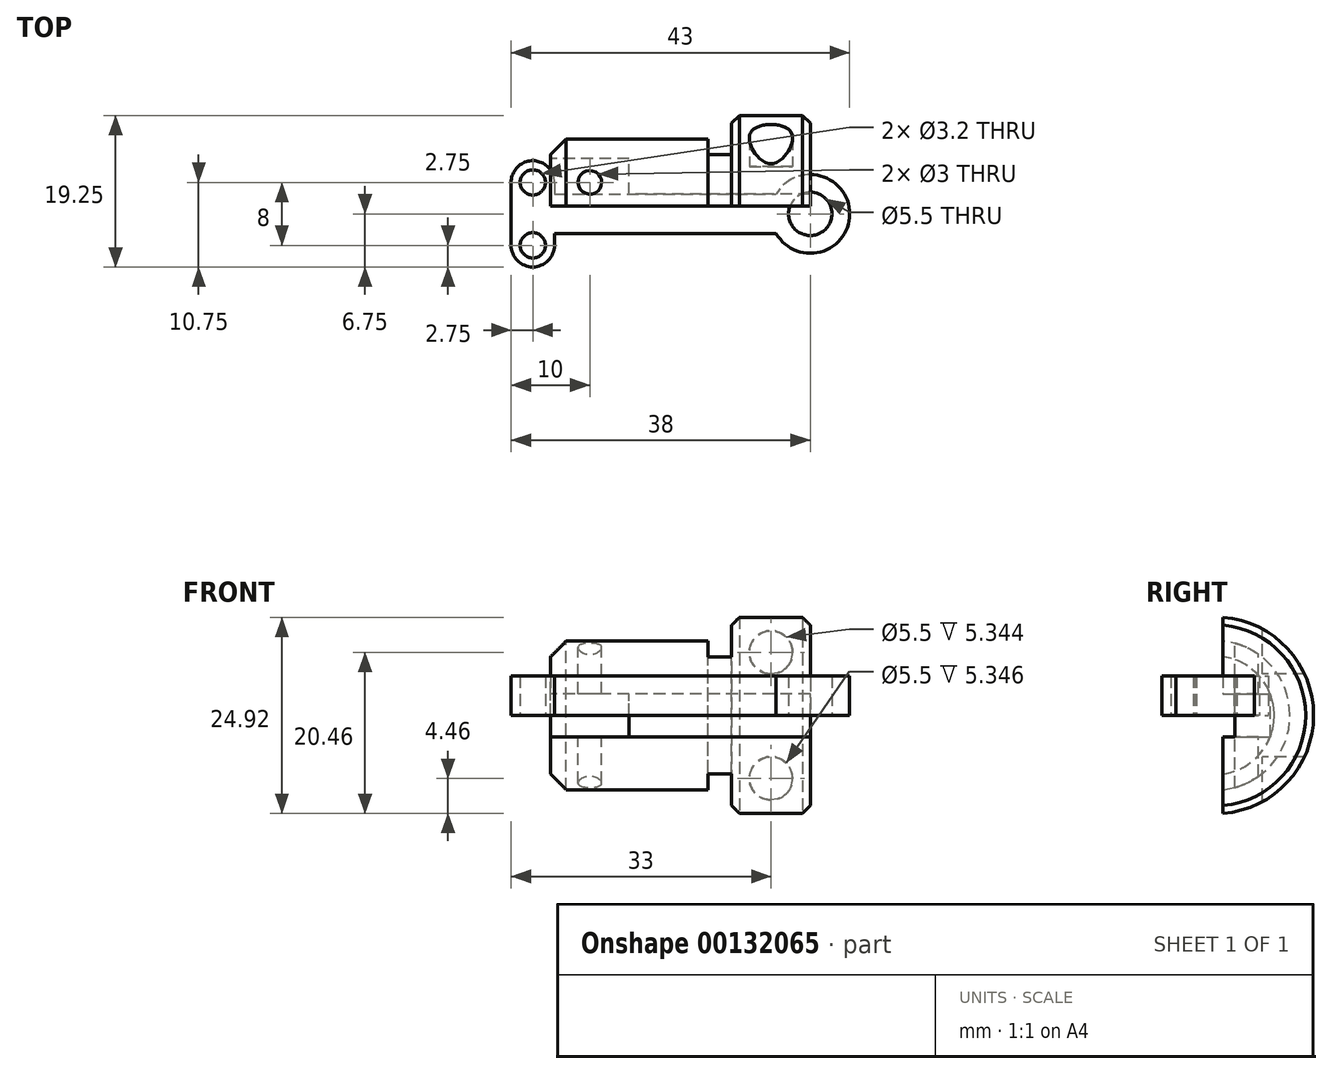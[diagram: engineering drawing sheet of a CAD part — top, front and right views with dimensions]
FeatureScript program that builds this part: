
annotation { "Feature Type Name" : "Feature", "Feature Type Description" : "" }
export const myFeature = defineFeature(function(context is Context, id is Id, definition is map)
    precondition{}
    {
        {
            var Q0;
            Q0=qCreatedBy(makeId("Front.planeOp"),FACE);
            var sketch = newSketch(context, id + "F0", { "sketchPlane" : qUnion([Q0])});
            skLineSegment(sketch, "E0", {"start": v(0, 0) * mm, "end": v(-33, 0) * mm});
            skLineSegment(sketch, "E1", {"start": v(-33, 0) * mm, "end": v(-33, 9.5) * mm});
            skLineSegment(sketch, "E2", {"start": v(-33, 9.5) * mm, "end": v(-13, 9.5) * mm});
            skLineSegment(sketch, "E3", {"start": v(-10, 12.5) * mm, "end": v(0, 12.5) * mm});
            skLineSegment(sketch, "E4", {"start": v(0, 12.5) * mm, "end": v(0, 0) * mm});
            skLineSegment(sketch, "E5", {"start": v(-13, 9.5) * mm, "end": v(-13, 7.5) * mm});
            skLineSegment(sketch, "E6", {"start": v(-13, 7.5) * mm, "end": v(-10, 7.5) * mm});
            skLineSegment(sketch, "E7", {"start": v(-10, 12.5) * mm, "end": v(-10, 7.5) * mm});
            skSolve(sketch);
        }
        {
            var Q0;
            Q0=makeQuery(id+"F0.imprint","IMPRINT",FACE,{"disambiguationData":[TD([[makeQuery(id+"F0.imprint","IMPRINT",EDGE,{"derivedFrom":sQuery(id+"F0.wireOp",EDGE,"E0")}),-1.0]])]});
            var Q1;
            Q1=sQuery(id+"F0.wireOp",EDGE,"E0");
            revolve(context, id + "F1", {"entities" : qUnion([Q0]), "axis" : qUnion([Q1]), "revolveType" : RevolveType.ONE_DIRECTION, "angle" : 180 * degree});
        }
        {
            var Q0;
            Q0=makeQuery(id+"F1.opRevolve","SWEPT_FACE",FACE,{"disambiguationData":[OSD([sQuery(id+"F0.wireOp",EDGE,"E4")])]});
            var sketch = newSketch(context, id + "F2", { "sketchPlane" : qUnion([Q0])});
            skLineSegment(sketch, "E8.bottom", {"start": v(0, 12.5) * mm, "end": v(1, 12.5) * mm});
            skLineSegment(sketch, "E8.top", {"start": v(0, -17.5) * mm, "end": v(1, -17.5) * mm});
            skLineSegment(sketch, "E8.left", {"start": v(0, 12.5) * mm, "end": v(0, -17.5) * mm});
            skLineSegment(sketch, "E8.right", {"start": v(1, 12.5) * mm, "end": v(1, -17.5) * mm});
            skSolve(sketch);
        }
        {
            var Q0;
            {var subQ0=sQuery(id+"F2.wireOp",EDGE,"E8.left");Q0=makeQuery(id+"F2.imprint","IMPRINT",FACE,{"disambiguationData":[TD([[makeQuery(id+"F2.imprint","IMPRINT",EDGE,{"derivedFrom":subQ0}),-1.0]])]});}
            extrude(context, id + "F3", {"entities" : qUnion([Q0]), "operationType" : NewBodyOperationType.REMOVE, "endBound" : BoundingType.THROUGH_ALL, "oppositeDirection" : true, "depth" : 25 * mm});
        }
        {
            var Q0;
            Q0=makeQuery(id+"F1.opRevolve","SWEPT_FACE",FACE,{"disambiguationData":[OSD([sQuery(id+"F0.wireOp",EDGE,"E1")])]});
            var sketch = newSketch(context, id + "F4", { "sketchPlane" : qUnion([Q0])});
            skLineSegment(sketch, "E9.bottom", {"start": v(-1, -2.75) * mm, "end": v(-7, -2.75) * mm});
            skLineSegment(sketch, "E9.top", {"start": v(-1, 2.75) * mm, "end": v(-7, 2.75) * mm});
            skLineSegment(sketch, "E9.left", {"start": v(-1, -2.75) * mm, "end": v(-1, 2.75) * mm});
            skLineSegment(sketch, "E9.right", {"start": v(-7, -2.75) * mm, "end": v(-7, 2.75) * mm});
            skSolve(sketch);
        }
        {
            var Q0;
            Q0=makeQuery(id+"F4.imprint","IMPRINT",FACE,{"disambiguationData":[TD([[makeQuery(id+"F4.imprint","IMPRINT",EDGE,{"derivedFrom":sQuery(id+"F4.wireOp",EDGE,"E9.bottom")}),-1.0]])]});
            extrude(context, id + "F5", {"entities" : qUnion([Q0]), "operationType" : NewBodyOperationType.REMOVE, "oppositeDirection" : true, "depth" : 10 * mm});
        }
        {
            var Q0;
            Q0=makeQuery(id+"F5.boolean.opBoolean","COPY",FACE,{"derivedFrom":makeQuery(id+"F5.opExtrude","CAP_FACE",FACE,{"disambiguationData":[OSD([sQuery(id+"F4.wireOp",EDGE,"E9.bottom"),sQuery(id+"F4.wireOp",EDGE,"E9.top"),sQuery(id+"F4.wireOp",EDGE,"E9.left"),sQuery(id+"F4.wireOp",EDGE,"E9.right")])],"isStart":false})});
            var sketch = newSketch(context, id + "F6", { "sketchPlane" : qUnion([Q0])});
            skLineSegment(sketch, "E10.bottom", {"start": v(-1, -2.75) * mm, "end": v(-2.5, -2.75) * mm});
            skLineSegment(sketch, "E10.top", {"start": v(-1, 2.75) * mm, "end": v(-4, 2.75) * mm});
            skLineSegment(sketch, "E10.left", {"start": v(-1, -2.75) * mm, "end": v(-1, 2.75) * mm});
            skLineSegment(sketch, "E10.right", {"start": v(-2.5, -2.75) * mm, "end": v(-2.5, 2.75) * mm});
            skSolve(sketch);
        }
        {
            var Q0;
            Q0=makeQuery(id+"F6.imprint","IMPRINT",FACE,{"disambiguationData":[TD([[makeQuery(id+"F6.imprint","IMPRINT",EDGE,{"derivedFrom":sQuery(id+"F6.wireOp",EDGE,"E10.bottom")}),-1.0]])]});
            extrude(context, id + "F7", {"entities" : qUnion([Q0]), "operationType" : NewBodyOperationType.REMOVE, "endBound" : BoundingType.THROUGH_ALL, "oppositeDirection" : true, "depth" : 25 * mm});
        }
        {
            var Q0;
            Q0=makeQuery(id+"F1.opRevolve","SWEPT_EDGE",EDGE,{"disambiguationData":[OSD([sQuery(id+"F0.wireOp",EDGE,"E1"),sQuery(id+"F0.wireOp",EDGE,"E2")])]});
            chamfer(context, id + "F8", {"entities" : qUnion([Q0]), "width" : 2 * mm, "tangentPropagation" : true});
        }
        {
            var Q0;
            Q0=qCreatedBy(makeId("Top.planeOp"),FACE);
            var sketch = newSketch(context, id + "F9", { "sketchPlane" : qUnion([Q0])});
            skCircle(sketch, "E11", {"center": v(-28, 4) * mm, "radius": 1.5 * mm});
            skSolve(sketch);
        }
        {
            var Q0;
            Q0 = qSketchRegion(id + "F9", true);
            extrude(context, id + "F10", {"entities" : qUnion([Q0]), "operationType" : NewBodyOperationType.REMOVE, "endBound" : BoundingType.SYMMETRIC, "oppositeDirection" : true, "depth" : 25 * mm});
        }
        {
            var Q0;
            Q0=qCreatedBy(makeId("Top.planeOp"),FACE);
            var sketch = newSketch(context, id + "F11", { "sketchPlane" : qUnion([Q0])});
            skArc(sketch, "E12", {"start": v(-4.33, -2.5) * mm, "mid": v(5, 0) * mm, "end": v(-4.33, 2.5) * mm});
            skCircle(sketch, "E13", {"center": v(0, 0) * mm, "radius": 2.75 * mm});
            skCircle(sketch, "E14", {"center": v(-35.25, 4) * mm, "radius": 1.6 * mm});
            skCircle(sketch, "E15", {"center": v(-35.25, -4) * mm, "radius": 1.6 * mm});
            skArc(sketch, "E16", {"start": v(-32.5, 4) * mm, "mid": v(-35.25, 6.75) * mm, "end": v(-38, 4) * mm});
            skArc(sketch, "E17", {"start": v(-38, -4) * mm, "mid": v(-35.25, -6.75) * mm, "end": v(-32.5, -4) * mm});
            skLineSegment(sketch, "E18", {"start": v(-38, 4) * mm, "end": v(-38, -4) * mm});
            skLineSegment(sketch, "E19", {"start": v(-32.5, 4) * mm, "end": v(-32.5, 2.5) * mm});
            skLineSegment(sketch, "E20", {"start": v(-32.5, -2.5) * mm, "end": v(-32.5, -4) * mm});
            skLineSegment(sketch, "E21.trimOffspring", {"start": v(-32.5, 2.5) * mm, "end": v(-4.33, 2.5) * mm});
            skLineSegment(sketch, "E22.trimOffspring", {"start": v(-32.5, -2.5) * mm, "end": v(-4.33, -2.5) * mm});
            skSolve(sketch);
        }
        {
            var Q0;
            Q0=makeQuery(id+"F11.imprint","IMPRINT",FACE,{"disambiguationData":[TD([[makeQuery(id+"F11.imprint","IMPRINT",EDGE,{"derivedFrom":sQuery(id+"F11.wireOp",EDGE,"E12")}),1.0]])]});
            extrude(context, id + "F12", {"entities" : qUnion([Q0]), "depth" : 5 * mm});
        }
        {
            var Q0;
            Q0=makeQuery(id+"F1.opRevolve","SWEPT_EDGE",EDGE,{"disambiguationData":[OSD([sQuery(id+"F0.wireOp",EDGE,"E3"),sQuery(id+"F0.wireOp",EDGE,"E7")])]});
            var Q1;
            Q1=makeQuery(id+"F1.opRevolve","SWEPT_EDGE",EDGE,{"disambiguationData":[OSD([sQuery(id+"F0.wireOp",EDGE,"E3"),sQuery(id+"F0.wireOp",EDGE,"E4")])]});
            chamfer(context, id + "F13", {"entities" : qUnion([Q0, Q1]), "width" : 1 * mm, "tangentPropagation" : true});
        }
        {
            var Q0;
            Q0=qCreatedBy(makeId("Front.planeOp"),FACE);
            cPlane(context, id + "F14", {"entities" : qUnion([Q0]), "cplaneType" : CPlaneType.OFFSET, "offset" : 6 * mm, "oppositeDirection" : true, "width" : 150 * mm, "height" : 150 * mm});
        }
        {
            var Q0;
            Q0=qCreatedBy(id+"F14.planeOp",FACE);
            var sketch = newSketch(context, id + "F15", { "sketchPlane" : qUnion([Q0])});
            skCircle(sketch, "E23", {"center": v(-5, -8) * mm, "radius": 2.75 * mm});
            skCircle(sketch, "E24", {"center": v(-5, 8) * mm, "radius": 2.75 * mm});
            skSolve(sketch);
        }
        {
            var Q0;
            Q0 = qSketchRegion(id + "F15", true);
            extrude(context, id + "F16", {"entities" : qUnion([Q0]), "operationType" : NewBodyOperationType.REMOVE, "endBound" : BoundingType.UP_TO_NEXT, "oppositeDirection" : true, "depth" : 25 * mm});
        }
    });
